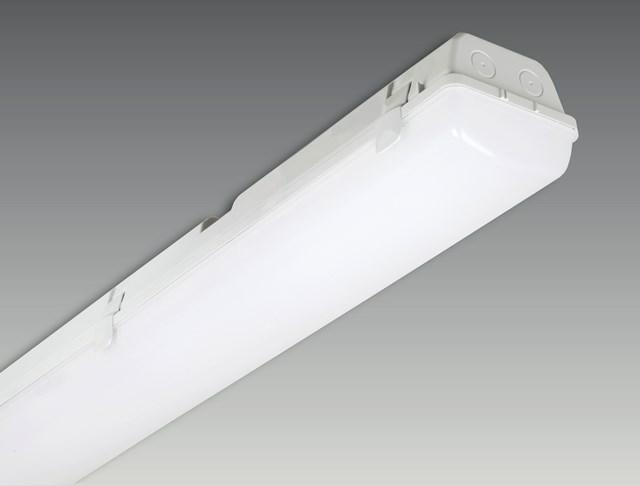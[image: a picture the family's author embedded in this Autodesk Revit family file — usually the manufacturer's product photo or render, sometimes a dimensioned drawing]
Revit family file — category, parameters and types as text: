
# Revit family: E1206UPM
name_source: partatom
category: Lighting Fixtures
revit_build: Autodesk Revit 2017 (Build: 20160225_1515(x64)
units: mm (PartAtom-declared; Revit-internal decimal feet)

## family parameters
Cut with Voids When Loaded = No
Host = Face
Light Source = Yes
Part Type = Normal
Room Calculation Point = No
Round Connector Dimension = Use Diameter
Shared = No

## types (2) — shared parameters
Apparent Load = 36 VA
Color Filter = 16777215
Default Elevation = 1219 mm
Dimming Lamp Color Temperature Shift = <None>
Emit Shape Visible in Rendering = No
Emit from Rectangle Length = 1250 mm  [stored 4.10105 ft]
Emit from Rectangle Width = 100 mm  [stored 0.328084 ft]
Lamp = LED
Manufacturer = ARLIGHT
Model = E1206UPM
Photometric Web File = E 1206 UPM-36W-4K(SG).IES
Tilt Angle = -90.00°
Type Comments = Industrial Lighting
Type Image = 1206.jpg
URL = http://www.arlight.net
Wattage Comments = 36W

## type names (no varying parameters)
- EUPM.1206.36.30
- EUPM.1206.36.40

note: [stored X ft] marks values corroborated as IEEE doubles in the binary element streams (Revit-internal decimal feet)

## geometry (parser evidence)
native form markers: Sweep x3
no freeform markers — native parametric forms only
